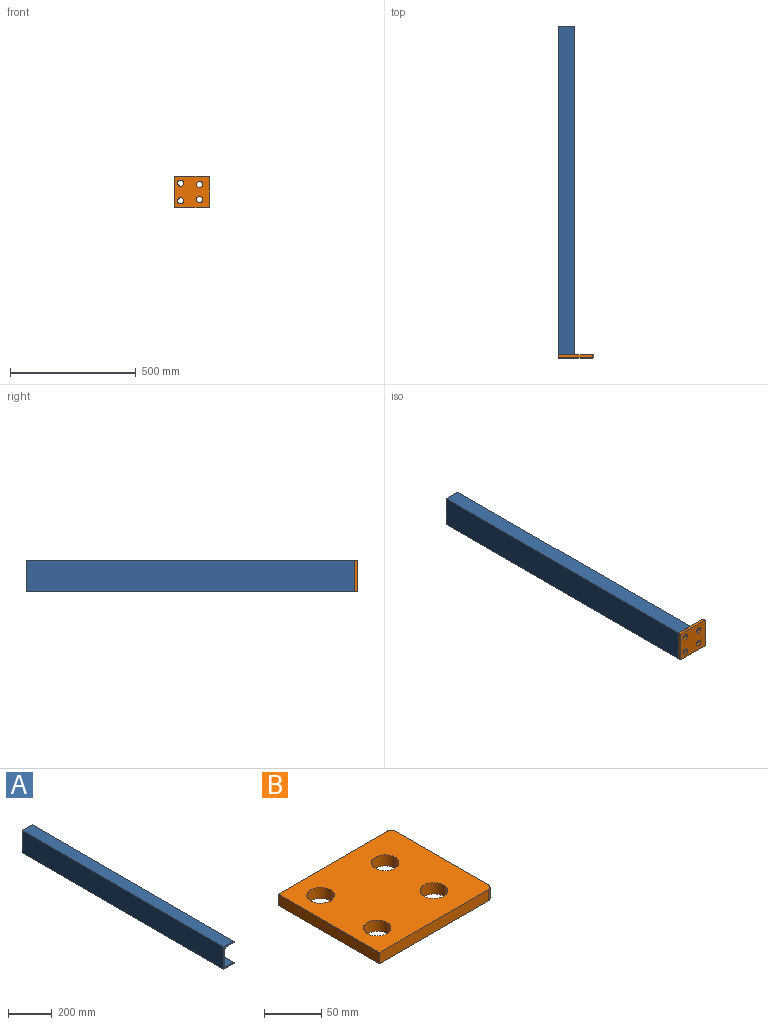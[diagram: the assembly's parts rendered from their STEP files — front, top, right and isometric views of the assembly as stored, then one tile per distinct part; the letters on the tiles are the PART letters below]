
ASSEMBLY  parts=2 mates=1
PART A: 12 faces, bbox 65x1308x125 mm
  f0: plane 1308x65mm, normal (0,0,1), area 85020mm2, adj f1,f9,f10,f11
  f1: plane 1308x125mm, normal (-1,0,0), area 163500mm2, adj f0,f2,f10,f11
  f2: plane 1308x65mm, normal (0,0,-1), area 85020mm2, adj f1,f3,f10,f11
  f3: plane 1308x7.5mm, normal (1,0,0), area 9810mm2, adj f2,f4,f10,f11
  f4: plane 1308x52.3mm, normal (0,0,1), area 68408.4mm2, adj f3,f5,f10,f11
  f5: cylinder r=8mm len=1308mm, axis (0,1,0), area 16436.8mm2, adj f4,f6,f10,f11
  f6: plane 1308x94mm, normal (1,0,0), area 122952mm2, adj f5,f7,f10,f11
  f7: cylinder r=8mm len=1308mm, axis (0,1,0), area 16436.8mm2, adj f6,f8,f10,f11
  f8: plane 1308x52.3mm, normal (0,0,-1), area 68408.4mm2, adj f7,f9,f10,f11
  f9: plane 1308x7.5mm, normal (1,0,0), area 9810mm2, adj f0,f8,f10,f11
  f10: plane 125x65mm, normal (0,-1,0), area 1519.5mm2, adj f0,f1,f2,f3,f4,f5,f6,f7
  f11: plane 125x65mm, normal (0,1,0), area 1519.5mm2, adj f0,f1,f2,f3,f4,f5,f6,f7
PART B: 12 faces, bbox 140x125x12 mm
  f0: plane 135x12mm, normal (0,1,0), area 1620mm2, adj f1,f8,f10,f11
  f1: plane 125x12mm, normal (-1,0,0), area 1500mm2, adj f0,f2,f10,f11
  f2: plane 135x12mm, normal (0,-1,0), area 1620mm2, adj f1,f3,f10,f11
  f3: cylinder r=5mm len=12mm, axis (0,0,-1), area 94.2mm2, adj f2,f4,f10,f11
  f4: plane 115x12mm, normal (1,0,0), area 1380mm2, adj f3,f8,f10,f11
  f5: cylinder r=12mm len=24mm, axis (0,0,-1), area 904.8mm2, adj f10,f11
  f6: cylinder r=12mm len=24mm, axis (0,0,-1), area 904.8mm2, adj f10,f11
  f7: cylinder r=12mm len=24mm, axis (0,0,-1), area 904.8mm2, adj f10,f11
  f8: cylinder r=5mm len=12mm, axis (0,0,-1), area 94.2mm2, adj f0,f4,f10,f11
  f9: cylinder r=12mm len=24mm, axis (0,0,-1), area 904.8mm2, adj f10,f11
  f10: plane 140x125mm, normal (0,0,1), area 15679.7mm2, adj f0,f1,f2,f3,f4,f5,f6,f7
  f11: plane 140x125mm, normal (0,0,-1), area 15679.7mm2, adj f0,f1,f2,f3,f4,f5,f6,f7
PLACE A t=(-533.83,211.24,-208.17)mm
PLACE B rot(axis=(-1,0,0),90deg) t=(-533.83,-1108.76,-208.17)mm
MATE fastened B.f1 <-> A.f1  axis (-1,0,0) through (-559,-1096.76,-208.17)mm
